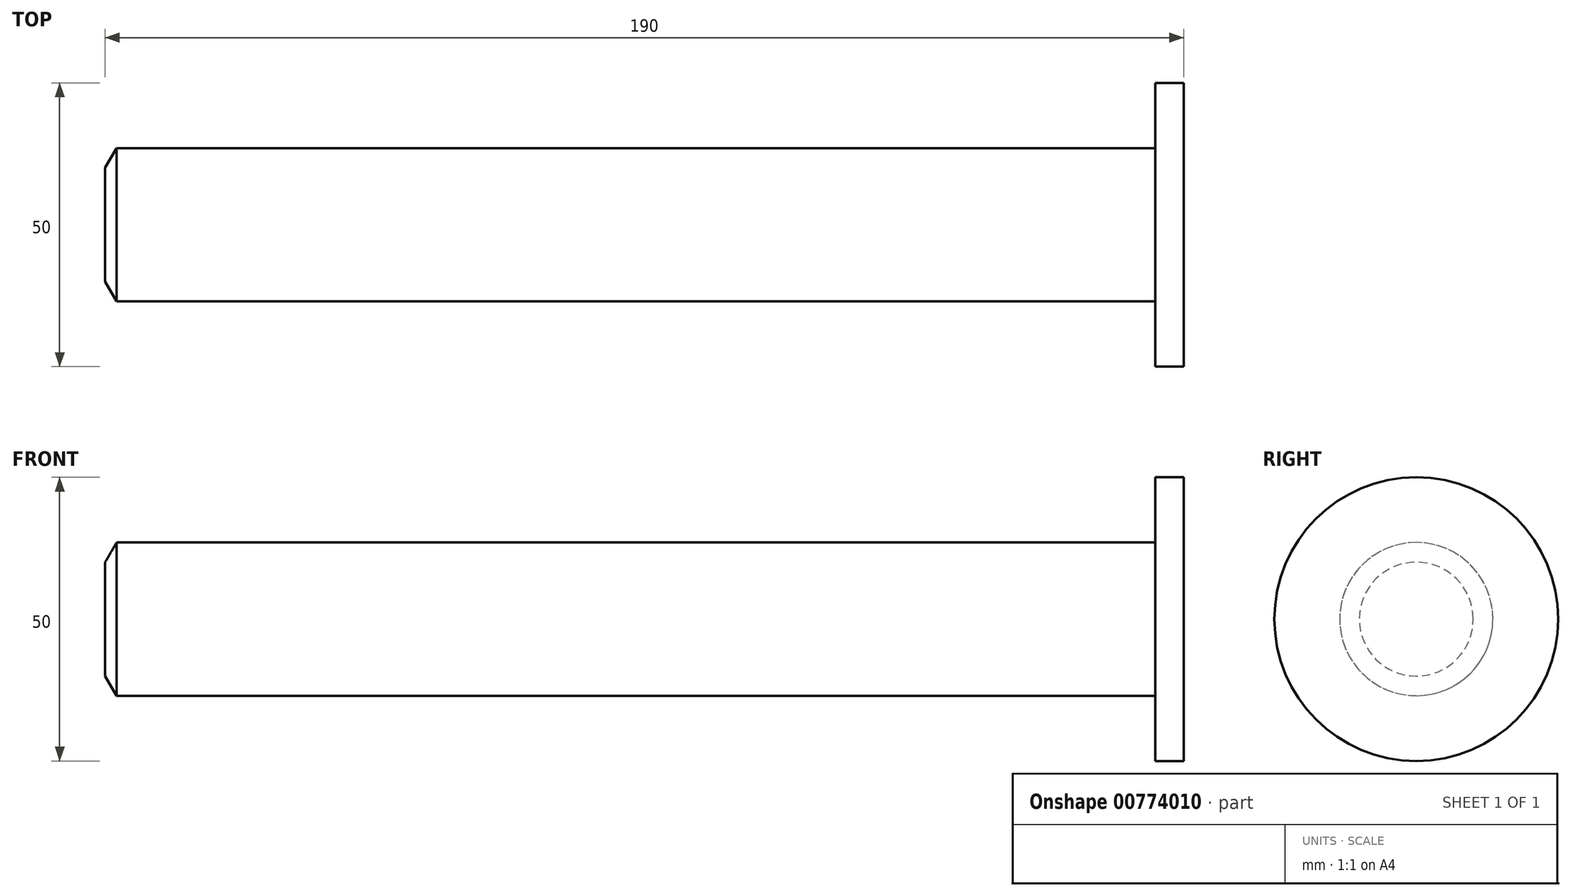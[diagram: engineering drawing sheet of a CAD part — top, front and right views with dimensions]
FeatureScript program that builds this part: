
annotation { "Feature Type Name" : "Feature", "Feature Type Description" : "" }
export const myFeature = defineFeature(function(context is Context, id is Id, definition is map)
    precondition{}
    {
        {
            var Q0;
            Q0=qCreatedBy(makeId("Right.planeOp"),FACE);
            var sketch = newSketch(context, id + "F0", { "sketchPlane" : qUnion([Q0])});
            skCircle(sketch, "E0", {"center": v(0, 0) * mm, "radius": 25 * mm});
            skCircle(sketch, "E1", {"center": v(0, 0) * mm, "radius": 13.5 * mm});
            skSolve(sketch);
        }
        {
            var Q0;
            Q0=makeQuery(id+"F0.imprint","IMPRINT",FACE,{"disambiguationData":[TD([[makeQuery(id+"F0.imprint","IMPRINT",EDGE,{"derivedFrom":sQuery(id+"F0.wireOp",EDGE,"E1")}),1.0]])]});
            extrude(context, id + "F1", {"entities" : qUnion([Q0]), "oppositeDirection" : true, "depth" : 190 * mm, "offsetDistance" : 25 * mm});
        }
        {
            var Q0;
            Q0 = qSketchRegion(id + "F0", true);
            extrude(context, id + "F2", {"entities" : qUnion([Q0]), "operationType" : NewBodyOperationType.ADD, "oppositeDirection" : true, "depth" : 5 * mm, "offsetDistance" : 25 * mm});
        }
        {
            var Q0;
            Q0=makeQuery(id+"F1.opExtrude","SWEPT_FACE",FACE,{"disambiguationData":[OSD([sQuery(id+"F0.wireOp",EDGE,"E1")])]});
            cPlane(context, id + "F3", {"entities" : qUnion([Q0]), "cplaneType" : CPlaneType.LINE_ANGLE, "offset" : 25 * mm, "angle" : 0 * degree, "width" : 150 * mm, "height" : 150 * mm});
        }
        {
            var Q0;
            Q0=qCreatedBy(id+"F3.planeOp",FACE);
            var sketch = newSketch(context, id + "F4", { "sketchPlane" : qUnion([Q0])});
            skLineSegment(sketch, "E2", {"start": v(188, 13.5) * mm, "end": v(190, 13.5) * mm});
            skLineSegment(sketch, "E3", {"start": v(188, 13.5) * mm, "end": v(190, 10.04) * mm});
            skLineSegment(sketch, "E4", {"start": v(190, 10.04) * mm, "end": v(190, 13.5) * mm});
            skLineSegment(sketch, "E5", {"start": v(188, 13.5) * mm, "end": v(185.5, 13.5) * mm, "construction": true});
            skLineSegment(sketch, "E6", {"start": v(188, 13.5) * mm, "end": v(185.4, 18.01) * mm, "construction": true});
            skLineSegment(sketch, "E7", {"start": v(0, 0) * mm, "end": v(190, 0) * mm, "construction": true});
            skLineSegment(sketch, "E8", {"start": v(190, 13.5) * mm, "end": v(190, 0) * mm, "construction": true});
            skSolve(sketch);
        }
        {
            var Q0;
            Q0 = qSketchRegion(id + "F4", true);
            var Q1;
            Q1=sQuery(id+"F4.wireOp",EDGE,"E7");
            revolve(context, id + "F5", {"operationType" : NewBodyOperationType.REMOVE, "surfaceOperationType" : NewSurfaceOperationType.NEW, "entities" : qUnion([Q0]), "axis" : qUnion([Q1]), "revolveType" : RevolveType.FULL, "oppositeDirection" : true});
        }
    });
